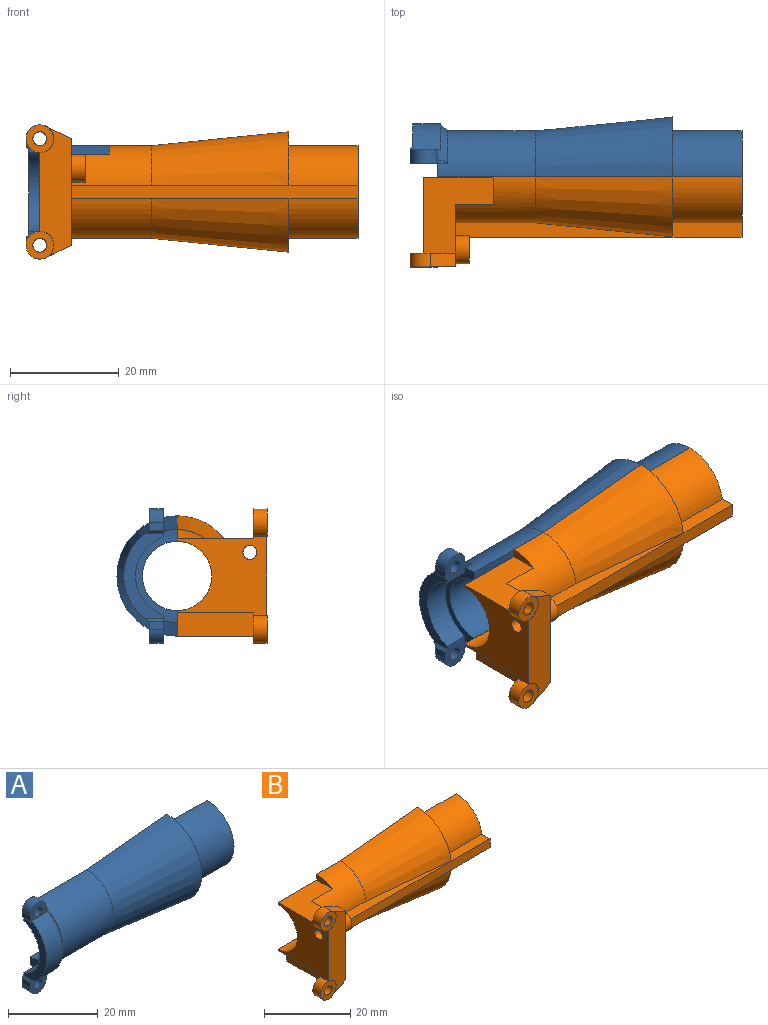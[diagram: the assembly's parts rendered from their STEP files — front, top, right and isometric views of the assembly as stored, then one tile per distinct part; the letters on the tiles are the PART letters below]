
ASSEMBLY  parts=2 mates=1
PART A: 29 faces, bbox 61x11.1x24.7 mm
  f0: plane 6.86x5.13mm, normal (0,1,0), area 19.4mm2, adj f2,f3,f11,f15,f20,f21,f25,f26
  f1: plane 2.54x1.42mm, normal (-1,0,0), area 3.6mm2, adj f16,f17,f19,f28
  f2: plane 2.54x1.42mm, normal (-1,0,0), area 3.6mm2, adj f0,f20,f22,f27
  f3: cylinder r=7.62mm len=14.37mm, axis (1,0,0), area 85.8mm2, adj f0,f15,f16,f26
  f4: plane 1.89x0.83mm, normal (1,0,0), area 0.7mm2, adj f20,f22,f24
  f5: plane 55.88x4.7mm, normal (0,1,0), area 152.7mm2, adj f6,f7,f8,f9,f10,f11,f15
  f6: cylinder r=6.35mm len=55.88mm, axis (-1,0,0), area 1114.8mm2, adj f5,f7,f12,f15
  f7: plane 17.02x8.51mm, normal (1,0,0), area 50.4mm2, adj f5,f6,f8,f12
  f8: cylinder r=8.51mm len=17.02mm, axis (-1,0,0), area 339.5mm2, adj f5,f7,f9,f12
  f9: plane 22.1x11.05mm, normal (1,0,0), area 78mm2, adj f5,f8,f10,f12
  f10: cone r=11.05mm half-angle=5.7deg, axis (1,0,0), area 780.3mm2, adj f5,f9,f11,f12
  f11: cylinder r=8.51mm len=17.91mm, axis (-1,0,0), area 440.4mm2, adj f0,f5,f10,f12,f15,f16,f23,f24
  f12: plane 55.88x4.7mm, normal (0,1,0), area 152.7mm2, adj f6,f7,f8,f9,f10,f11,f15
  f13: cylinder r=9.78mm len=16.71mm, axis (-1,0,0), area 102.3mm2, adj f19,f22,f24,f26,f27,f28
  f14: plane 1.89x0.83mm, normal (1,0,0), area 0.7mm2, adj f17,f19,f24
  f15: plane 17.02x7.62mm, normal (-1,0,0), area 32.5mm2, adj f0,f3,f5,f6,f11,f12,f16
  f16: plane 6.86x5.13mm, normal (0,1,0), area 19.4mm2, adj f1,f3,f11,f15,f17,f18,f23,f26
  f17: cylinder r=2.54mm len=5.08mm, axis (0,1,0), area 20.2mm2, adj f1,f14,f16,f19,f23
  f18: cylinder r=1.27mm len=2.54mm, axis (0,1,0), area 20.3mm2, adj f16,f19
  f19: plane 5.6x3.97mm, normal (0,-1,0), area 12.4mm2, adj f1,f13,f14,f17,f18,f24
  f20: cylinder r=2.54mm len=5.08mm, axis (0,1,0), area 20.2mm2, adj f0,f2,f4,f22,f25
  f21: cylinder r=1.27mm len=2.54mm, axis (0,1,0), area 20.3mm2, adj f0,f22
  f22: plane 5.6x3.97mm, normal (0,-1,0), area 12.4mm2, adj f2,f4,f13,f20,f21,f24
  f23: bspline ~1.81x1.78mm, area 1mm2, adj f11,f16,f17,f24
  f24: cone r=10.29mm half-angle=45deg, axis (-1,0,0), area 44.3mm2, adj f4,f11,f13,f14,f19,f22,f23,f25
  f25: bspline ~1.81x1.78mm, area 1mm2, adj f0,f11,f20,f24
  f26: plane 15.7x7.24mm, normal (-1,0,0), area 41.8mm2, adj f0,f3,f13,f16,f27,f28
  f27: plane 3.31x0.53mm, normal (-0.71,0,0.71), area 2.1mm2, adj f0,f2,f13,f26
  f28: plane 3.31x0.53mm, normal (-0.71,0,-0.71), area 2.1mm2, adj f1,f13,f16,f26
PART B: 41 faces, bbox 61x16.6x24.7 mm
  f0: cylinder r=8.51mm len=14.66mm, axis (-1,0,0), area 177.3mm2, adj f1,f5,f22,f37
  f1: cone r=11.05mm half-angle=5.7deg, axis (1,0,0), area 357.5mm2, adj f0,f5,f17,f37
  f2: cylinder r=8.51mm len=12.7mm, axis (-1,0,0), area 153.6mm2, adj f5,f15,f17,f35
  f3: plane 10.98x9.78mm, normal (1,0,0), area 35.8mm2, adj f6,f16,f18,f33
  f4: plane 16.43x14.48mm, normal (-1,0,0), area 157.8mm2, adj f5,f6,f8,f11,f14,f21,f28,f29
  f5: plane 58.43x4.71mm, normal (0,1,0), area 156.9mm2, adj f0,f1,f2,f4,f14,f15,f17,f22
  f6: plane 58.42x4.7mm, normal (0,1,0), area 137.3mm2, adj f3,f4,f10,f14,f15,f16,f18,f30
  f7: plane 16.44x4.52mm, normal (0.44,0,-0.9), area 57.4mm2, adj f8,f9,f21,f26,f27,f29
  f8: cylinder r=2.54mm len=5.08mm, axis (0,1,0), area 24.1mm2, adj f4,f7,f20,f21,f29
  f9: plane 16.44x0.02mm, normal (0,0,-1), area 0.2mm2, adj f7,f21,f22
  f10: cylinder r=8.51mm len=14.66mm, axis (-1,0,0), area 140mm2, adj f6,f18,f22,f30,f31,f36
  f11: cylinder r=2.54mm len=5.08mm, axis (0,1,0), area 24.1mm2, adj f4,f19,f21,f25,f32
  f12: cylinder r=1.27mm len=2.54mm, axis (0,1,0), area 15.4mm2, adj f19,f23,f32
  f13: cylinder r=1.27mm len=2.54mm, axis (0,1,0), area 15.4mm2, adj f20,f24,f29
  f14: cylinder r=6.35mm len=58.42mm, axis (-1,0,0), area 1165.4mm2, adj f4,f5,f6,f15
  f15: plane 17.02x11.05mm, normal (1,0,0), area 56.9mm2, adj f2,f5,f6,f14,f16,f33,f34,f35
  f16: cylinder r=8.51mm len=12.7mm, axis (-1,0,0), area 153.6mm2, adj f3,f6,f15,f33
  f17: plane 10.98x9.78mm, normal (1,0,0), area 35.8mm2, adj f1,f2,f5,f35
  f18: cone r=11.05mm half-angle=5.7deg, axis (1,0,0), area 357.5mm2, adj f3,f6,f10,f36
  f19: plane 5.08x5.08mm, normal (0,-1,0), area 15.2mm2, adj f11,f12
  f20: plane 5.08x5.08mm, normal (0,-1,0), area 15.2mm2, adj f8,f13
  f21: plane 23.98x5.79mm, normal (0,-1,0), area 109.1mm2, adj f4,f7,f8,f9,f11,f22,f25
  f22: plane 19.55x16.44mm, normal (1,0,0), area 145.8mm2, adj f0,f5,f9,f10,f21,f25,f31,f32
  f23: cylinder r=1.27mm len=2.46mm, axis (0,-1,0), area 4.9mm2, adj f12,f32
  f24: cylinder r=1.27mm len=2.46mm, axis (0,-1,0), area 4.9mm2, adj f13,f29
  f25: plane 4.54x2.46mm, normal (0.44,0,0.9), area 12.4mm2, adj f11,f21,f22,f32
  f26: plane 2.91x1.42mm, normal (0,1,0), area 2mm2, adj f5,f7,f27
  f27: plane 13.97x4.42mm, normal (-1,0,0), area 61.8mm2, adj f5,f7,f26,f28,f29
  f28: plane 13.97x2.88mm, normal (0,0,-1), area 40.2mm2, adj f4,f5,f27,f29
  f29: plane 5.55x5.42mm, normal (0,1,0), area 19.7mm2, adj f4,f7,f8,f13,f24,f27,f28
  f30: plane 5.03x1.64mm, normal (-1,0,0), area 5.6mm2, adj f6,f10,f31
  f31: plane 13.97x12.73mm, normal (0,0,1), area 115.8mm2, adj f4,f6,f10,f22,f30,f32
  f32: plane 8.33x5.45mm, normal (0,1,0), area 30mm2, adj f4,f11,f12,f22,f23,f25,f31
  f33: plane 12.71x2.64mm, normal (0,0,1), area 33.5mm2, adj f3,f15,f16,f34,f36
  f34: plane 52.63x2.54mm, normal (0,-1,0), area 133.4mm2, adj f15,f22,f33,f35,f36,f37
  f35: plane 12.71x2.64mm, normal (0,0,-1), area 33.5mm2, adj f2,f15,f17,f34,f37
  f36: plane 39.97x2.68mm, normal (0,0,1), area 72.8mm2, adj f10,f18,f22,f33,f34
  f37: plane 39.97x2.68mm, normal (0,0,-1), area 72.8mm2, adj f0,f1,f22,f34,f35
  f38: cylinder r=1.27mm len=8.33mm, axis (-1,0,0), area 66.5mm2, adj f4,f40
  f39: cylinder r=2.54mm len=5.08mm, axis (-1,0,0), area 40.5mm2, adj f22,f40
  f40: plane 5.08x5.08mm, normal (1,0,0), area 15.2mm2, adj f38,f39
PLACE A rot(axis=(1,0,0),180deg) t=(-5.66,-16.64,2.39)mm
PLACE B t=(-5.66,-16.64,-17.17)mm
MATE fastened A.f12 <-> B.f5  axis (0,-1,0) through (52.76,-16.64,-14.82)mm
